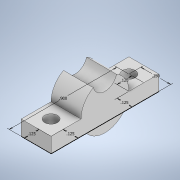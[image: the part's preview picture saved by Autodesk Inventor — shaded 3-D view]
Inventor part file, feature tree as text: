
AUTODESK INVENTOR PART (.ipt)
format: ipt  version: 2020 (Build 240168000, 168)  size: 126,976 bytes
history: native  units: in
note: dims shown in document units (in); Inventor stores cm internally (conversion verified against a paired STEP export)
features: sketch x2, extrude x2, hole x1
ambient origin geometry x8: Origin, YZ Plane, XZ Plane, XY Plane, X Axis, Y Axis, Z Axis, Center Point
bodies: Solid1 (feature_tree)
feature tree (5):
  sketch  "Sketch1"  dims[d0=0.25in d1=0.9in]
  extrude  "Extrusion1"  Depth=0.9in
  hole  "Hole1"  [1 undecoded]
  extrude  "Extrusion2"  Depth=0.125in
  sketch  "Sketch2"  dims[d2=0.125in d3=0.125in d4=0.125in d5=0.125in d6=0.125in d7=0.0in d8=0.1065in d9=0.75in d10=0.375in d11=0.25in d12=0.5635in d13=0.25in d14=0.0in d15=0.4in d16=0.2in d17=0.25in d18=0.0in]
note: 1 required parameter value undecoded (feature->parameter linkage not recoverable at this tier; creation-order binding heuristic only, values carry confidence <= 0.55)
